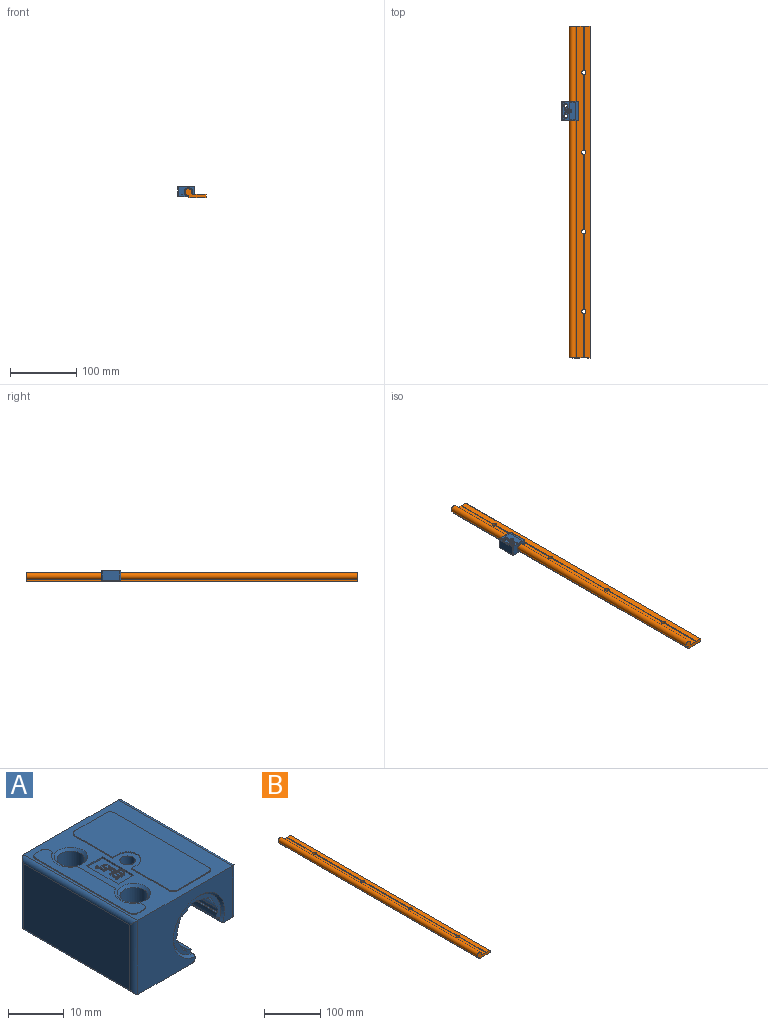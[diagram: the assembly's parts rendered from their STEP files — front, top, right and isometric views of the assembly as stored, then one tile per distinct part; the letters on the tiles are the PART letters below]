
ASSEMBLY  parts=2 mates=1
PART A: 223 faces, bbox 26x29x16.5 mm
  f0: cylinder r=5mm len=28mm, axis (0,1,0), area 73.3mm2, adj f176,f204,f212,f214
  f1: cylinder r=5mm len=28mm, axis (0,1,0), area 73.3mm2, adj f176,f209,f212,f218
  f2: cone r=2.75mm half-angle=45deg, axis (0,0,-1), area 12.2mm2, adj f3,f124
  f3: cylinder r=2.5mm len=11.8mm, axis (0,0,1), area 185.4mm2, adj f2,f4
  f4: cone r=2.75mm half-angle=45deg, axis (0,0,1), area 12.2mm2, adj f3,f161
  f5: cone r=2.75mm half-angle=45deg, axis (0,0,-1), area 12.2mm2, adj f6,f123
  f6: cylinder r=2.5mm len=11.8mm, axis (0,0,1), area 185.4mm2, adj f5,f7
  f7: cone r=2.75mm half-angle=45deg, axis (0,0,1), area 12.2mm2, adj f6,f161
  f8: cylinder r=1.4mm len=4.05mm, axis (0,0,1), area 27.7mm2, adj f9,f161
  f9: cylinder r=6.9mm len=13.8mm, axis (0,1,0), area 95mm2, adj f8,f20,f125,f126,f163
  f10: cone r=6.25mm half-angle=45deg, axis (0,1,0), area 21.8mm2, adj f21,f22,f127,f129,f131,f132,f133,f212
  f11: cone r=6.25mm half-angle=45deg, axis (0,-1,0), area 21.8mm2, adj f18,f19,f113,f128,f130,f164,f165,f176
  f12: cylinder r=4.75mm len=9.5mm, axis (0,0,1), area 104.5mm2, adj f124,f162
  f13: cylinder r=4.75mm len=9.5mm, axis (0,0,1), area 104.5mm2, adj f123,f162
  f14: cylinder r=0.1mm len=0.2mm, axis (0,0,1), area 0.1mm2, adj f87,f105
  f15: cylinder r=0.68mm len=1.35mm, axis (0,0,1), area 0.3mm2, adj f25,f40,f108
  f16: cylinder r=0.28mm len=0.55mm, axis (0,0,1), area 0.3mm2, adj f23,f105
  f17: cylinder r=0.25mm len=0.5mm, axis (0,0,1), area 0.2mm2, adj f23,f103
  f18: cylinder r=6mm len=12.5mm, axis (0,1,0), area 5.4mm2, adj f11,f20,f128,f173
  f19: cylinder r=6mm len=12.5mm, axis (0,1,0), area 5.4mm2, adj f11,f20,f165,f172
  f20: plane 13.8x13.73mm, normal (0,1,0), area 14.9mm2, adj f9,f18,f19,f126,f128,f130,f163,f164
  f21: cylinder r=6mm len=12.5mm, axis (0,1,0), area 5.4mm2, adj f10,f125,f132,f172
  f22: cylinder r=6mm len=12.5mm, axis (0,1,0), area 5.4mm2, adj f10,f125,f127,f173
  f23: plane 0.55x0.55mm, normal (0,0,1), area 0mm2, adj f16,f17
  f24: plane 0.15x0.15mm, normal (-1,0,0), area 0mm2, adj f32,f40,f41,f105
  f25: plane 1.35x0.15mm, normal (-1,0,0), area 0.2mm2, adj f15,f40,f108
  f26: plane 1.35x0.15mm, normal (-1,0,0), area 0.2mm2, adj f37,f40,f52,f105
  f27: plane 0.26x0.15mm, normal (-1,0,0), area 0mm2, adj f33,f35,f40,f105
  f28: plane 0.15x0.15mm, normal (1,0,0), area 0mm2, adj f32,f39,f40,f105
  f29: plane 1.34x0.15mm, normal (1,0,0), area 0.2mm2, adj f38,f40,f107
  f30: plane 1.35x0.15mm, normal (1,0,0), area 0.2mm2, adj f36,f40,f106
  f31: plane 0.24x0.15mm, normal (1,0,0), area 0mm2, adj f33,f34,f40,f105
  f32: plane 0.15x0.03mm, normal (0,-1,0), area 0mm2, adj f24,f28,f40,f105
  f33: plane 0.15x0.03mm, normal (0,1,0), area 0mm2, adj f27,f31,f40,f105
  f34: cylinder r=0.45mm len=0.75mm, axis (0,0,1), area 0.2mm2, adj f31,f40,f66,f105
  f35: cylinder r=0.45mm len=0.31mm, axis (0,0,1), area 0.1mm2, adj f27,f40,f65,f105
  f36: cylinder r=0.68mm len=1.35mm, axis (0,0,1), area 0.3mm2, adj f30,f40,f106
  f37: plane 0.88x0.15mm, normal (0,1,0), area 0.1mm2, adj f26,f40,f51,f105
  f38: cylinder r=0.68mm len=1.34mm, axis (0,0,1), area 0.3mm2, adj f29,f40,f107
  f39: plane 0.75x0.15mm, normal (0,-1,0), area 0.1mm2, adj f28,f40,f86,f105
  f40: plane 5x2.53mm, normal (0,0,1), area 3.1mm2, adj f15,f24,f25,f26,f27,f28,f29,f30
  f41: plane 0.9x0.15mm, normal (0,-1,0), area 0.1mm2, adj f24,f40,f42,f105
  f42: plane 0.15x0.15mm, normal (-1,0,0), area 0mm2, adj f40,f41,f43,f105
  f43: plane 0.88x0.15mm, normal (0,1,0), area 0.1mm2, adj f40,f42,f44,f105
  f44: plane 0.15x0.03mm, normal (-1,0,0), area 0mm2, adj f40,f43,f45,f105
  f45: cylinder r=0.81mm len=1.51mm, axis (0,0,1), area 0.3mm2, adj f40,f44,f46,f105
  f46: plane 0.35x0.15mm, normal (0,-1,0), area 0.1mm2, adj f40,f45,f47,f105
  f47: plane 0.15x0.15mm, normal (-1,0,0), area 0mm2, adj f40,f46,f48,f105
  f48: plane 0.88x0.15mm, normal (0,1,0), area 0.1mm2, adj f40,f47,f49,f105
  f49: plane 0.15x0.03mm, normal (-1,0,0), area 0mm2, adj f40,f48,f50,f105
  f50: plane 0.88x0.15mm, normal (0,-1,0), area 0.1mm2, adj f40,f49,f51,f105
  f51: plane 0.15x0.15mm, normal (-1,0,0), area 0mm2, adj f37,f40,f50,f105
  f52: cylinder r=0.68mm len=0.15mm, axis (0,0,1), area 0mm2, adj f26,f40,f53,f105
  f53: plane 0.83x0.15mm, normal (0,-1,0), area 0.1mm2, adj f40,f52,f54,f105
  f54: plane 0.15x0.15mm, normal (-1,0,0), area 0mm2, adj f40,f53,f55,f105
  f55: plane 0.88x0.15mm, normal (0,1,0), area 0.1mm2, adj f40,f54,f56,f105
  f56: plane 0.3x0.15mm, normal (-1,0,0), area 0mm2, adj f40,f55,f57,f105
  f57: cylinder r=0.49mm len=0.43mm, axis (0,0,1), area 0.1mm2, adj f40,f56,f58,f105
  f58: cylinder r=0.4mm len=0.45mm, axis (0,0,1), area 0.1mm2, adj f40,f57,f59,f105
  f59: plane 0.38x0.15mm, normal (-1,0,0), area 0.1mm2, adj f40,f58,f60,f105
  f60: cylinder r=0.35mm len=0.35mm, axis (0,0,1), area 0.1mm2, adj f40,f59,f61,f105
  f61: plane 0.15x0.15mm, normal (1,0,0), area 0mm2, adj f40,f60,f62,f105
  f62: cylinder r=0.26mm len=0.25mm, axis (0,0,1), area 0.1mm2, adj f40,f61,f63,f105
  f63: plane 0.28x0.15mm, normal (1,0,0), area 0mm2, adj f40,f62,f64,f105
  f64: cylinder r=0.3mm len=0.6mm, axis (0,0,1), area 0.1mm2, adj f40,f63,f65,f105
  f65: plane 0.28x0.15mm, normal (-1,0,0), area 0mm2, adj f35,f40,f64,f105
  f66: plane 0.4x0.15mm, normal (1,0,0), area 0.1mm2, adj f34,f40,f67,f105
  f67: cylinder r=0.35mm len=0.35mm, axis (0,0,1), area 0.1mm2, adj f40,f66,f68,f105
  f68: plane 0.15x0.15mm, normal (-1,0,0), area 0mm2, adj f40,f67,f69,f105
  f69: cylinder r=0.26mm len=0.25mm, axis (0,0,1), area 0.1mm2, adj f40,f68,f70,f105
  f70: plane 0.35x0.15mm, normal (-1,0,0), area 0.1mm2, adj f40,f69,f71,f105
  f71: cylinder r=0.3mm len=0.6mm, axis (0,0,1), area 0.1mm2, adj f40,f70,f72,f105
  f72: plane 0.78x0.15mm, normal (1,0,0), area 0.1mm2, adj f40,f71,f73,f105
  f73: plane 0.75x0.15mm, normal (0,1,0), area 0.1mm2, adj f40,f72,f74,f105
  f74: plane 0.15x0.15mm, normal (1,0,0), area 0mm2, adj f40,f73,f75,f105
  f75: plane 0.35x0.15mm, normal (0,-1,0), area 0.1mm2, adj f40,f74,f76,f105
  f76: cylinder r=0.8mm len=1.5mm, axis (0,0,1), area 0.3mm2, adj f40,f75,f77,f105
  f77: plane 0.15x0.03mm, normal (1,0,0), area 0mm2, adj f40,f76,f78,f105
  f78: plane 0.75x0.15mm, normal (0,1,0), area 0.1mm2, adj f40,f77,f79,f105
  f79: cylinder r=0.82mm len=1.65mm, axis (0,0,1), area 0.4mm2, adj f40,f78,f80,f105
  f80: plane 0.15x0.15mm, normal (-1,0,0), area 0mm2, adj f40,f79,f81,f105
  f81: cylinder r=0.68mm len=1.35mm, axis (0,0,1), area 0.3mm2, adj f40,f80,f82,f105
  f82: plane 0.4x0.15mm, normal (0,-1,0), area 0.1mm2, adj f40,f81,f83,f105
  f83: cylinder r=0.79mm len=1.5mm, axis (0,0,1), area 0.3mm2, adj f40,f82,f84,f105
  f84: plane 0.15x0.03mm, normal (1,0,0), area 0mm2, adj f40,f83,f85,f105
  f85: plane 0.75x0.15mm, normal (0,1,0), area 0.1mm2, adj f40,f84,f86,f105
  f86: plane 0.15x0.15mm, normal (1,0,0), area 0mm2, adj f39,f40,f85,f105
  f87: plane 0.2x0.2mm, normal (0,0,1), area 0mm2, adj f14
  f88: plane 0.15x0.15mm, normal (0,1,0), area 0mm2, adj f89,f91,f102,f104
  f89: plane 0.15x0.06mm, normal (1,0,0), area 0mm2, adj f88,f90,f102,f104
  f90: cylinder r=0.07mm len=0.15mm, axis (0,0,1), area 0mm2, adj f89,f91,f102,f104
  f91: plane 0.15x0.06mm, normal (-1,0,0), area 0mm2, adj f88,f90,f102,f104
  f92: plane 0.18x0.15mm, normal (0,1,0), area 0mm2, adj f93,f101,f102,f103
  f93: plane 0.15x0.01mm, normal (1,0,0), area 0mm2, adj f92,f94,f102,f103
  f94: plane 0.35x0.15mm, normal (0,-1,0), area 0.1mm2, adj f93,f95,f102,f103
  f95: plane 0.15x0.08mm, normal (-1,0,0), area 0mm2, adj f94,f96,f102,f103
  f96: cylinder r=0.09mm len=0.18mm, axis (0,0,1), area 0mm2, adj f95,f97,f102,f103
  f97: plane 0.15x0.01mm, normal (1,0,0), area 0mm2, adj f96,f98,f102,f103
  f98: plane 0.18x0.15mm, normal (-0.5,0.87,0), area 0mm2, adj f97,f99,f102,f103
  f99: plane 0.15x0.01mm, normal (1,0,0), area 0mm2, adj f98,f100,f102,f103
  f100: plane 0.18x0.15mm, normal (0.5,-0.87,0), area 0mm2, adj f99,f101,f102,f103
  f101: plane 0.15x0.04mm, normal (1,0,0), area 0mm2, adj f92,f100,f102,f103
  f102: plane 0.35x0.16mm, normal (0,0,1), area 0mm2, adj f88,f89,f90,f91,f92,f93,f94,f95
  f103: plane 0.5x0.5mm, normal (0,0,1), area 0.2mm2, adj f17,f92,f93,f94,f95,f96,f97,f98
  f104: plane 0.15x0.14mm, normal (0,0,1), area 0mm2, adj f88,f89,f90,f91
  f105: plane 8x4mm, normal (0,0,1), area 26.6mm2, adj f14,f16,f24,f26,f27,f28,f31,f32
  f106: plane 1.35x0.6mm, normal (0,0,1), area 0.6mm2, adj f30,f36
  f107: plane 1.34x0.6mm, normal (0,0,1), area 0.6mm2, adj f29,f38
  f108: plane 1.35x0.73mm, normal (0,0,1), area 0.8mm2, adj f15,f25
  f109: cylinder r=1mm len=11.3mm, axis (0,0,1), area 16.2mm2, adj f110,f111,f131,f160
  f110: cylinder r=1mm len=29mm, axis (0,1,0), area 44mm2, adj f109,f111,f112,f126
  f111: plane 27x9.3mm, normal (1,0,0), area 251.1mm2, adj f109,f110,f112,f160
  f112: cylinder r=1mm len=11.3mm, axis (0,0,1), area 16.2mm2, adj f110,f111,f113,f160
  f113: plane 24x16.3mm, normal (0,-1,0), area 232.2mm2, adj f11,f112,f117,f118,f126,f130,f161,f162
  f114: cylinder r=1mm len=16.24mm, axis (0,0,1), area 24mm2, adj f115,f116,f118,f131
  f115: cylinder r=1mm len=29mm, axis (0,1,0), area 44mm2, adj f114,f116,f117,f161
  f116: plane 27x14.3mm, normal (-1,0,0), area 386.1mm2, adj f114,f115,f117,f118
  f117: cylinder r=1mm len=16.24mm, axis (0,0,1), area 24mm2, adj f113,f115,f116,f118
  f118: cylinder r=1.53mm len=29mm, axis (0,1,0), area 55.1mm2, adj f113,f114,f116,f117,f131,f162
  f119: plane 4x0.3mm, normal (0,1,0), area 1.2mm2, adj f105,f120,f122,f161
  f120: plane 8x0.3mm, normal (1,0,0), area 2.4mm2, adj f105,f119,f121,f161
  f121: plane 4x0.3mm, normal (0,-1,0), area 1.2mm2, adj f105,f120,f122,f161
  f122: plane 8x0.3mm, normal (-1,0,0), area 2.4mm2, adj f105,f119,f121,f161
  f123: plane 9.5x9.5mm, normal (0,0,-1), area 42.6mm2, adj f5,f13
  f124: plane 9.5x9.5mm, normal (0,0,-1), area 42.6mm2, adj f2,f12
  f125: plane 13.8x13.73mm, normal (0,-1,0), area 14.9mm2, adj f9,f21,f22,f126,f127,f129,f132,f133
  f126: plane 29x2.37mm, normal (0,0,-1), area 67.8mm2, adj f9,f20,f110,f113,f125,f129,f130,f131
  f127: cylinder r=0.5mm len=12.91mm, axis (0,1,0), area 8.6mm2, adj f10,f22,f125,f129
  f128: cylinder r=0.5mm len=12.91mm, axis (0,1,0), area 8.6mm2, adj f11,f18,f20,f130
  f129: plane 13x0.18mm, normal (-0.5,0,-0.87), area 2.7mm2, adj f10,f125,f126,f127,f131
  f130: plane 13x0.18mm, normal (-0.5,0,-0.87), area 2.7mm2, adj f11,f20,f113,f126,f128
  f131: plane 24x16.3mm, normal (0,1,0), area 232.2mm2, adj f10,f109,f114,f118,f126,f129,f133,f161
  f132: cylinder r=0.5mm len=12.91mm, axis (0,1,0), area 8.6mm2, adj f10,f21,f125,f133
  f133: plane 13x0.15mm, normal (1,0,0), area 2mm2, adj f10,f125,f131,f132,f163
  f134: cylinder r=3.5mm len=6.32mm, axis (0,0,-1), area 1.6mm2, adj f135,f145,f146,f161
  f135: plane 9.68x0.2mm, normal (1,0,0), area 1.9mm2, adj f134,f136,f146,f161
  f136: cylinder r=3.5mm len=6.32mm, axis (0,0,-1), area 1.6mm2, adj f135,f137,f146,f161
  f137: plane 0.84x0.2mm, normal (1,0,0), area 0.2mm2, adj f136,f138,f146,f161
  f138: cylinder r=1mm len=1mm, axis (0,0,-1), area 0.3mm2, adj f137,f139,f146,f161
  f139: plane 1.5x0.2mm, normal (0,1,0), area 0.3mm2, adj f138,f140,f146,f161
  f140: cylinder r=1mm len=1mm, axis (0,0,-1), area 0.3mm2, adj f139,f141,f146,f161
  f141: plane 24x0.2mm, normal (-1,0,0), area 4.8mm2, adj f140,f142,f146,f161
  f142: cylinder r=1mm len=1mm, axis (0,0,-1), area 0.3mm2, adj f141,f143,f146,f161
  f143: plane 1.5x0.2mm, normal (0,-1,0), area 0.3mm2, adj f142,f144,f146,f161
  f144: cylinder r=1mm len=1mm, axis (0,0,-1), area 0.3mm2, adj f143,f145,f146,f161
  f145: plane 0.84x0.2mm, normal (1,0,0), area 0.2mm2, adj f134,f144,f146,f161
  f146: plane 26x3.5mm, normal (0,0,1), area 72mm2, adj f134,f135,f136,f137,f138,f139,f140,f141
  f147: cylinder r=1mm len=1mm, axis (0,0,-1), area 0.3mm2, adj f148,f158,f159,f161
  f148: plane 24x0.2mm, normal (1,0,0), area 4.8mm2, adj f147,f149,f159,f161
  f149: cylinder r=1mm len=1mm, axis (0,0,-1), area 0.3mm2, adj f148,f150,f159,f161
  f150: plane 8x0.2mm, normal (0,1,0), area 1.6mm2, adj f149,f151,f159,f161
  f151: cylinder r=1mm len=1mm, axis (0,0,-1), area 0.3mm2, adj f150,f152,f159,f161
  f152: plane 9.6x0.2mm, normal (-1,0,0), area 1.9mm2, adj f151,f153,f159,f161
  f153: plane 1.4x0.2mm, normal (0,-1,0), area 0.3mm2, adj f152,f154,f159,f161
  f154: cylinder r=2.4mm len=4.8mm, axis (0,0,-1), area 1.5mm2, adj f153,f155,f159,f161
  f155: plane 1.4x0.2mm, normal (0,1,0), area 0.3mm2, adj f154,f156,f159,f161
  f156: plane 9.6x0.2mm, normal (-1,0,0), area 1.9mm2, adj f155,f157,f159,f161
  f157: cylinder r=1mm len=1mm, axis (0,0,-1), area 0.3mm2, adj f156,f158,f159,f161
  f158: plane 8x0.2mm, normal (0,-1,0), area 1.6mm2, adj f147,f157,f159,f161
  f159: plane 26x10mm, normal (0,0,1), area 243.4mm2, adj f147,f148,f149,f150,f151,f152,f153,f154
  f160: cylinder r=1mm len=29mm, axis (0,1,0), area 44mm2, adj f109,f111,f112,f161
  f161: plane 29x24mm, normal (0,0,1), area 285.9mm2, adj f4,f7,f8,f113,f115,f119,f120,f121
  f162: plane 29x13.1mm, normal (0,0,-1), area 238.1mm2, adj f12,f13,f113,f118,f131,f163
  f163: cylinder r=1mm len=29mm, axis (0,1,0), area 44.5mm2, adj f9,f20,f113,f125,f131,f133,f162,f164
  f164: plane 13x0.15mm, normal (1,0,0), area 2mm2, adj f11,f20,f113,f163,f165
  f165: cylinder r=0.5mm len=12.91mm, axis (0,1,0), area 8.6mm2, adj f11,f19,f20,f164
  f166: cylinder r=6mm len=3mm, axis (0,1,0), area 4.7mm2, adj f20,f125,f187,f188
  f167: cylinder r=6mm len=3mm, axis (0,1,0), area 4.7mm2, adj f20,f125,f184,f185
  f168: cylinder r=6mm len=3mm, axis (0,1,0), area 4.7mm2, adj f20,f125,f182,f198
  f169: cylinder r=6mm len=3mm, axis (0,1,0), area 4.7mm2, adj f20,f125,f195,f196
  f170: cylinder r=6mm len=3mm, axis (0,1,0), area 4.7mm2, adj f20,f125,f192,f193
  f171: cylinder r=6mm len=3mm, axis (0,1,0), area 4.7mm2, adj f20,f125,f190,f191
  f172: plane 28x1.64mm, normal (0.97,0,-0.26), area 30.1mm2, adj f19,f20,f21,f125,f174,f176,f203,f212
  f173: plane 28x1.64mm, normal (-0.26,0,-0.97), area 30.1mm2, adj f18,f20,f22,f125,f175,f176,f200,f212
  f174: cylinder r=6.7mm len=3mm, axis (0,1,0), area 4.8mm2, adj f20,f125,f172,f191
  f175: cylinder r=6.7mm len=3mm, axis (0,1,0), area 4.8mm2, adj f20,f125,f173,f192
  f176: plane 12x11.75mm, normal (0,-1,0), area 23.2mm2, adj f0,f1,f11,f172,f173,f199,f200,f201
  f177: plane 1.5x0.76mm, normal (-0.87,0,-0.5), area 1.3mm2, adj f178,f179,f181,f183
  f178: plane 2.17x1.76mm, normal (0,-1,0), area 1.6mm2, adj f177,f180,f181,f183
  f179: plane 2.17x1.76mm, normal (0,1,0), area 1.6mm2, adj f177,f180,f181,f183
  f180: plane 1.5x0.76mm, normal (0.87,0,0.5), area 1.3mm2, adj f178,f179,f181,f183
  f181: plane 1.73x1.5mm, normal (-0.5,0,0.87), area 3mm2, adj f177,f178,f179,f180
  f182: plane 3x0.68mm, normal (0.97,0,0.26), area 2.1mm2, adj f20,f125,f168,f183
  f183: cylinder r=6.7mm len=3mm, axis (0,1,0), area 7.5mm2, adj f20,f125,f177,f178,f179,f180,f182,f184
  f184: plane 3x0.5mm, normal (-0.71,0,-0.71), area 2.1mm2, adj f20,f125,f167,f183
  f185: plane 3x0.61mm, normal (0.5,0,0.87), area 2.1mm2, adj f20,f125,f167,f186
  f186: cylinder r=6.7mm len=3.35mm, axis (0,1,0), area 10.5mm2, adj f20,f125,f185,f187
  f187: plane 3x0.7mm, normal (0,0,-1), area 2.1mm2, adj f20,f125,f166,f186
  f188: plane 3x0.68mm, normal (-0.26,0,0.97), area 2.1mm2, adj f20,f125,f166,f189
  f189: cylinder r=6.7mm len=3mm, axis (0,1,0), area 10.5mm2, adj f20,f125,f188,f190
  f190: plane 3x0.5mm, normal (0.71,0,-0.71), area 2.1mm2, adj f20,f125,f171,f189
  f191: plane 3x0.61mm, normal (-0.87,0,0.5), area 2.1mm2, adj f20,f125,f171,f174
  f192: plane 3x0.7mm, normal (0,0,1), area 2.1mm2, adj f20,f125,f170,f175
  f193: plane 3x0.68mm, normal (0.26,0,-0.97), area 2.1mm2, adj f20,f125,f170,f194
  f194: cylinder r=6.7mm len=3mm, axis (0,1,0), area 10.5mm2, adj f20,f125,f193,f195
  f195: plane 3x0.5mm, normal (-0.71,0,0.71), area 2.1mm2, adj f20,f125,f169,f194
  f196: plane 3x0.61mm, normal (0.87,0,-0.5), area 2.1mm2, adj f20,f125,f169,f197
  f197: cylinder r=6.7mm len=3.35mm, axis (0,1,0), area 10.5mm2, adj f20,f125,f196,f198
  f198: plane 3x0.7mm, normal (-1,0,0), area 2.1mm2, adj f20,f125,f168,f197
  f199: cylinder r=5mm len=28mm, axis (0,1,0), area 73.3mm2, adj f176,f207,f212,f220
  f200: cylinder r=5mm len=28mm, axis (0,1,0), area 32mm2, adj f173,f176,f208,f212
  f201: cylinder r=5mm len=28mm, axis (0,1,0), area 73.3mm2, adj f176,f206,f212,f222
  f202: cylinder r=5mm len=28mm, axis (0,1,0), area 73.3mm2, adj f176,f205,f211,f212
  f203: cylinder r=5mm len=28mm, axis (0,1,0), area 32mm2, adj f172,f176,f212,f216
  f204: plane 28x0.21mm, normal (0.71,0,-0.71), area 8.4mm2, adj f0,f176,f212,f215
  f205: plane 28x0.3mm, normal (0,0,-1), area 8.4mm2, adj f176,f202,f212,f213
  f206: plane 28x0.21mm, normal (-0.71,0,-0.71), area 8.4mm2, adj f176,f201,f210,f212
  f207: plane 28x0.3mm, normal (-1,0,0), area 8.4mm2, adj f176,f199,f212,f221
  f208: plane 28x0.3mm, normal (0,0,1), area 8.4mm2, adj f176,f200,f212,f217
  f209: plane 28x0.21mm, normal (-0.71,0,0.71), area 8.4mm2, adj f1,f176,f212,f219
  f210: cylinder r=5.3mm len=28mm, axis (0,1,0), area 38.9mm2, adj f176,f206,f211,f212
  f211: plane 28x0.26mm, normal (0.5,0,0.87), area 8.4mm2, adj f176,f202,f210,f212
  f212: plane 12x11.75mm, normal (0,1,0), area 23.2mm2, adj f0,f1,f10,f172,f173,f199,f200,f201
  f213: cylinder r=5.3mm len=28mm, axis (0,1,0), area 38.9mm2, adj f176,f205,f212,f214
  f214: plane 28x0.29mm, normal (-0.26,0,0.97), area 8.4mm2, adj f0,f176,f212,f213
  f215: cylinder r=5.3mm len=28mm, axis (0,1,0), area 38.9mm2, adj f176,f204,f212,f216
  f216: plane 28x0.26mm, normal (-0.87,0,0.5), area 8.4mm2, adj f176,f203,f212,f215
  f217: cylinder r=5.3mm len=28mm, axis (0,1,0), area 38.9mm2, adj f176,f208,f212,f218
  f218: plane 28x0.29mm, normal (0.26,0,-0.97), area 8.4mm2, adj f1,f176,f212,f217
  f219: cylinder r=5.3mm len=28mm, axis (0,1,0), area 38.9mm2, adj f176,f209,f212,f220
  f220: plane 28x0.26mm, normal (0.87,0,-0.5), area 8.4mm2, adj f176,f199,f212,f219
  f221: cylinder r=5.3mm len=28mm, axis (0,1,0), area 38.9mm2, adj f176,f207,f212,f222
  f222: plane 28x0.29mm, normal (0.97,0,0.26), area 8.4mm2, adj f176,f201,f212,f221
PART B: 32 faces, bbox 32x500x14 mm
  f0: cylinder r=5mm len=500mm, axis (0,1,0), area 12821.5mm2, adj f19,f20,f30,f31
  f1: cylinder r=3.3mm len=6.6mm, axis (0,0,1), area 109.6mm2, adj f5,f10,f11,f12,f16,f17,f25
  f2: cylinder r=3.3mm len=6.6mm, axis (0,0,1), area 109.6mm2, adj f5,f8,f9,f10,f11,f12,f25
  f3: cylinder r=3.3mm len=6.6mm, axis (0,0,1), area 109.6mm2, adj f5,f6,f7,f8,f9,f12,f25
  f4: cylinder r=3.3mm len=6.6mm, axis (0,0,1), area 109.6mm2, adj f5,f6,f7,f12,f13,f14,f25
  f5: plane 500x9mm, normal (0,0,1), area 4444.7mm2, adj f1,f2,f3,f4,f6,f8,f10,f14
  f6: plane 113.48x0.5mm, normal (-0.5,0,0.87), area 65.5mm2, adj f3,f4,f5,f7
  f7: plane 113.48x0.5mm, normal (0.5,0,0.87), area 65.5mm2, adj f3,f4,f6,f12
  f8: plane 113.48x0.5mm, normal (-0.5,0,0.87), area 65.5mm2, adj f2,f3,f5,f9
  f9: plane 113.48x0.5mm, normal (0.5,0,0.87), area 65.5mm2, adj f2,f3,f8,f12
  f10: plane 113.48x0.5mm, normal (-0.5,0,0.87), area 65.5mm2, adj f1,f2,f5,f11
  f11: plane 113.48x0.5mm, normal (0.5,0,0.87), area 65.5mm2, adj f1,f2,f10,f12
  f12: plane 500x10.5mm, normal (0,0,1), area 5194.7mm2, adj f1,f2,f3,f4,f7,f9,f11,f13
  f13: plane 66.74x0.5mm, normal (0.5,0,0.87), area 38.5mm2, adj f4,f12,f14,f30
  f14: plane 66.74x0.5mm, normal (-0.5,0,0.87), area 38.5mm2, adj f4,f5,f13,f30
  f15: plane 500x0.5mm, normal (0.71,0,0.71), area 353.6mm2, adj f5,f29,f30,f31
  f16: plane 66.74x0.5mm, normal (-0.5,0,0.87), area 38.5mm2, adj f1,f5,f17,f31
  f17: plane 66.74x0.5mm, normal (0.5,0,0.87), area 38.5mm2, adj f1,f12,f16,f31
  f18: plane 500x1.43mm, normal (0.5,0,0.87), area 826.5mm2, adj f12,f19,f30,f31
  f19: cylinder r=0.3mm len=500mm, axis (0,1,0), area 228mm2, adj f0,f18,f30,f31
  f20: cylinder r=0.3mm len=500mm, axis (0,1,0), area 227.1mm2, adj f0,f21,f30,f31
  f21: plane 500x3.21mm, normal (-1,0,0), area 1604.2mm2, adj f20,f22,f30,f31
  f22: plane 500x0.5mm, normal (-0.71,0,-0.71), area 353.6mm2, adj f21,f23,f30,f31
  f23: plane 500x10.5mm, normal (0,0,-1), area 5250mm2, adj f22,f24,f30,f31
  f24: plane 500x0.2mm, normal (0.71,0,-0.71), area 141.4mm2, adj f23,f25,f30,f31
  f25: plane 500x11.6mm, normal (0,0,-1), area 5663.2mm2, adj f1,f2,f3,f4,f24,f26,f30,f31
  f26: plane 500x0.2mm, normal (-0.71,0,-0.71), area 141.4mm2, adj f25,f27,f30,f31
  f27: plane 500x3.5mm, normal (0,0,-1), area 1750mm2, adj f26,f28,f30,f31
  f28: plane 500x0.5mm, normal (0.71,0,-0.71), area 353.6mm2, adj f27,f29,f30,f31
  f29: plane 500x4.5mm, normal (1,0,0), area 2250mm2, adj f15,f28,f30,f31
  f30: plane 32x14mm, normal (0,1,0), area 221.7mm2, adj f0,f5,f12,f13,f14,f15,f18,f19
  f31: plane 32x14mm, normal (0,-1,0), area 221.7mm2, adj f0,f5,f12,f15,f16,f17,f18,f19
PLACE A t=(-22.04,107.5,3.5)mm
PLACE B t=(4.96,-250,-5.5)mm
MATE cylindrical A.f0 <-> B.f0  axis (0,1,0) through (-22.04,122,3.5)mm
